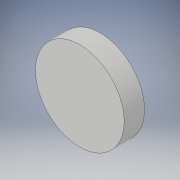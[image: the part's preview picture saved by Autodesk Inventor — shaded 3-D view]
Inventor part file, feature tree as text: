
AUTODESK INVENTOR PART (.ipt)
format: ipt  version: 2019 (Build 230136000, 136)  size: 90,624 bytes
history: native  units: mm
features: other x1, extrude x1, sketch x1
ambient origin geometry x8: Origin, YZ Plane, XZ Plane, XY Plane, X Axis, Y Axis, Z Axis, Center Point
bodies: Body1 (feature_tree)
feature tree (3):
  other  "實體1"
  extrude  "擠出1"  Depth=43.5mm
  sketch  "草圖1"
